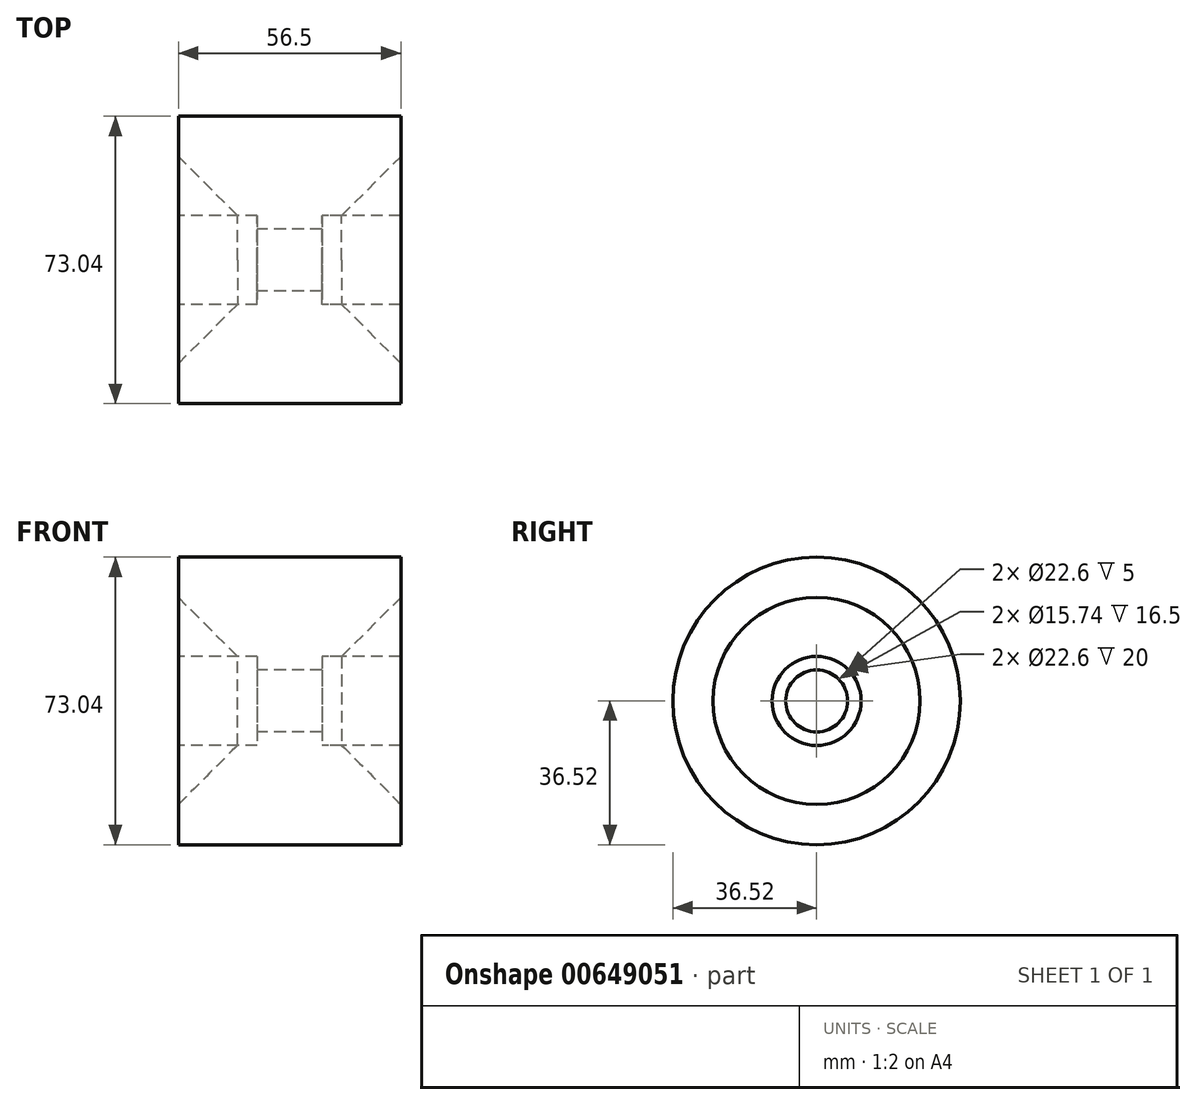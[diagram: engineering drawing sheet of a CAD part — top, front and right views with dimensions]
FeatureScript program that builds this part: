
annotation { "Feature Type Name" : "Feature", "Feature Type Description" : "" }
export const myFeature = defineFeature(function(context is Context, id is Id, definition is map)
    precondition{}
    {
        {
            var Q0;
            Q0=qCreatedBy(makeId("Top.planeOp"),FACE);
            var sketch = newSketch(context, id + "F0", { "sketchPlane" : qUnion([Q0])});
            skLineSegment(sketch, "E0.bottom", {"start": v(0, 36.52) * mm, "end": v(20, 36.52) * mm});
            skLineSegment(sketch, "E0.top", {"start": v(0, 11.3) * mm, "end": v(20, 11.3) * mm});
            skLineSegment(sketch, "E0.left", {"start": v(0, 36.52) * mm, "end": v(0, 11.3) * mm});
            skLineSegment(sketch, "E0.right", {"start": v(20, 36.52) * mm, "end": v(20, 11.3) * mm});
            skLineSegment(sketch, "E1.bottom", {"start": v(0, 36.52) * mm, "end": v(-16.5, 36.52) * mm});
            skLineSegment(sketch, "E1.left", {"start": v(0, 36.52) * mm, "end": v(0, 7.87) * mm});
            skLineSegment(sketch, "E1.right", {"start": v(-16.5, 36.52) * mm, "end": v(-16.5, 7.87) * mm});
            skLineSegment(sketch, "E2.bottom", {"start": v(-16.5, 36.52) * mm, "end": v(-36.5, 36.52) * mm});
            skLineSegment(sketch, "E2.top", {"start": v(-16.5, 11.3) * mm, "end": v(-36.5, 11.3) * mm});
            skLineSegment(sketch, "E2.left", {"start": v(-16.5, 36.52) * mm, "end": v(-16.5, 11.3) * mm});
            skLineSegment(sketch, "E2.right", {"start": v(-36.5, 36.52) * mm, "end": v(-36.5, 11.3) * mm});
            skLineSegment(sketch, "E3.MirrorCS", {"start": v(0, -36.52) * mm, "end": v(0, -11.3) * mm});
            skLineSegment(sketch, "E4.MirrorCS", {"start": v(-36.5, -36.52) * mm, "end": v(-36.5, -11.3) * mm});
            skLineSegment(sketch, "E5.MirrorCS", {"start": v(-16.5, -36.52) * mm, "end": v(-16.5, -11.3) * mm});
            skLineSegment(sketch, "E6.MirrorCS", {"start": v(-16.5, -11.3) * mm, "end": v(-36.5, -11.3) * mm});
            skLineSegment(sketch, "E7.MirrorCS", {"start": v(0, -36.52) * mm, "end": v(20, -36.52) * mm});
            skLineSegment(sketch, "E8.MirrorCS", {"start": v(0, -11.3) * mm, "end": v(20, -11.3) * mm});
            skLineSegment(sketch, "E9.MirrorCS", {"start": v(0, -36.52) * mm, "end": v(-16.5, -36.52) * mm});
            skLineSegment(sketch, "E10.MirrorCS", {"start": v(-16.5, -36.52) * mm, "end": v(-36.5, -36.52) * mm});
            skLineSegment(sketch, "E11.MirrorCS", {"start": v(-16.5, -36.52) * mm, "end": v(-16.5, -7.87) * mm});
            skLineSegment(sketch, "E12.MirrorCS", {"start": v(0, -36.52) * mm, "end": v(0, -7.87) * mm});
            skLineSegment(sketch, "E13.MirrorCS", {"start": v(20, -36.52) * mm, "end": v(20, -11.3) * mm});
            skLineSegment(sketch, "E14.bottom", {"start": v(0, -7.87) * mm, "end": v(-16.5, -7.87) * mm});
            skLineSegment(sketch, "E14.top", {"start": v(0, 7.87) * mm, "end": v(-16.5, 7.87) * mm});
            skPoint(sketch, "E14.middle", {"position": v(-8.25, 0) * mm});
            skPoint(sketch, "E14.right.start.orphan", {"position": v(-34.17, -7.87) * mm});
            skPoint(sketch, "E15.orphan", {"position": v(-34.17, 7.87) * mm});
            skPoint(sketch, "E16.orphan", {"position": v(-16.5, 0) * mm});
            skPoint(sketch, "E17.orphan", {"position": v(0, 0) * mm});
            skPoint(sketch, "E14.left.end.orphan", {"position": v(17.67, 7.87) * mm});
            skPoint(sketch, "E14.left.start.orphan", {"position": v(17.67, -7.87) * mm});
            skLineSegment(sketch, "E18", {"start": v(-55.95, 0) * mm, "end": v(50.74, 0) * mm, "construction": true});
            skSolve(sketch);
        }
        {
            var Q0;
            Q0 = qSketchRegion(id + "F0", true);
            var Q1;
            Q1=sQuery(id+"F0.wireOp",EDGE,"E18");
            revolve(context, id + "F1", {"entities" : qUnion([Q0]), "axis" : qUnion([Q1]), "revolveType" : RevolveType.FULL});
        }
        {
            var Q0;
            Q0=makeQuery(id+"F1.opRevolve","SWEPT_EDGE",EDGE,{"disambiguationData":[OSD([sQuery(id+"F0.wireOp",EDGE,"E0.top"),sQuery(id+"F0.wireOp",EDGE,"E0.right")])]});
            var Q1;
            Q1=makeQuery(id+"F1.opRevolve","SWEPT_EDGE",EDGE,{"disambiguationData":[OSD([sQuery(id+"F0.wireOp",EDGE,"E2.top"),sQuery(id+"F0.wireOp",EDGE,"E2.right")])]});
            chamfer(context, id + "F2", {"entities" : qUnion([Q0, Q1]), "width" : 15 * mm, "tangentPropagation" : true});
        }
    });
